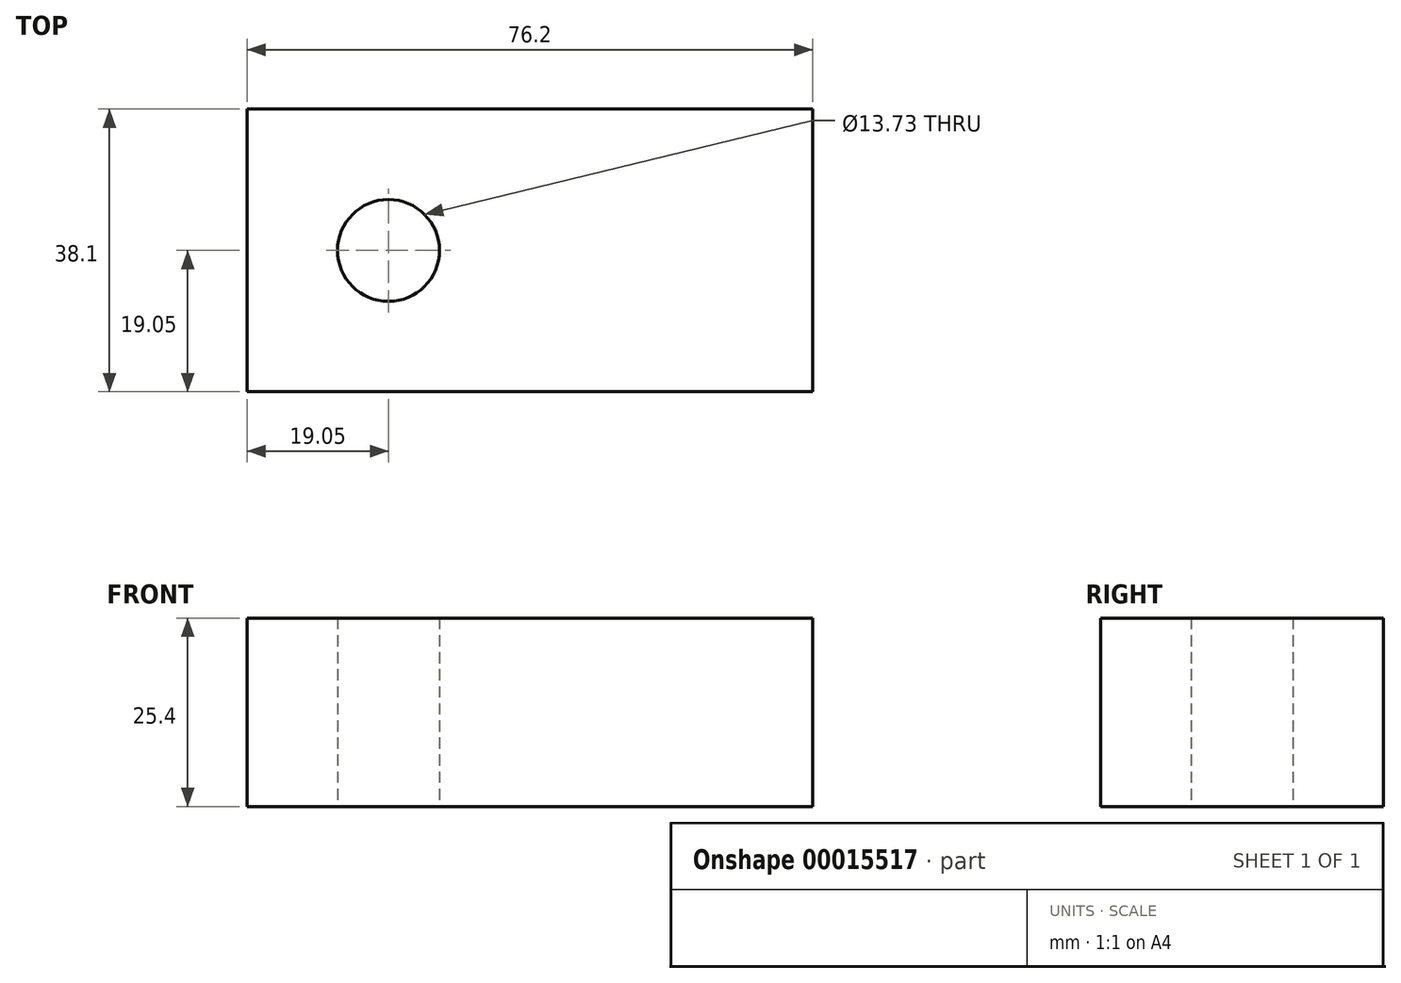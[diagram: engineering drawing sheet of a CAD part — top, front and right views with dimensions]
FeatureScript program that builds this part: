
annotation { "Feature Type Name" : "Feature", "Feature Type Description" : "" }
export const myFeature = defineFeature(function(context is Context, id is Id, definition is map)
    precondition{}
    {
        {
            var Q0;
            Q0=qCreatedBy(makeId("Top.planeOp"),FACE);
            var sketch = newSketch(context, id + "F0", { "sketchPlane" : qUnion([Q0])});
            skLineSegment(sketch, "E0", {"start": v(0, 0) * mm, "end": v(-76.2, 0) * mm});
            skLineSegment(sketch, "E1", {"start": v(-76.2, 0) * mm, "end": v(-76.2, 38.1) * mm});
            skLineSegment(sketch, "E2", {"start": v(-76.2, 38.1) * mm, "end": v(0, 38.1) * mm});
            skLineSegment(sketch, "E3", {"start": v(0, 38.1) * mm, "end": v(0, 0) * mm});
            skCircle(sketch, "E4", {"center": v(-57.15, 19.05) * mm, "radius": 6.86 * mm});
            skSolve(sketch);
        }
        {
            var Q0;
            Q0=makeQuery(id+"F0.imprint","IMPRINT",FACE,{"disambiguationData":[TD([[makeQuery(id+"F0.imprint","IMPRINT",EDGE,{"derivedFrom":sQuery(id+"F0.wireOp",EDGE,"E0")}),-1.0]])]});
            extrude(context, id + "F1", {"entities" : qUnion([Q0]), "depth" : 25.4 * mm});
        }
    });
